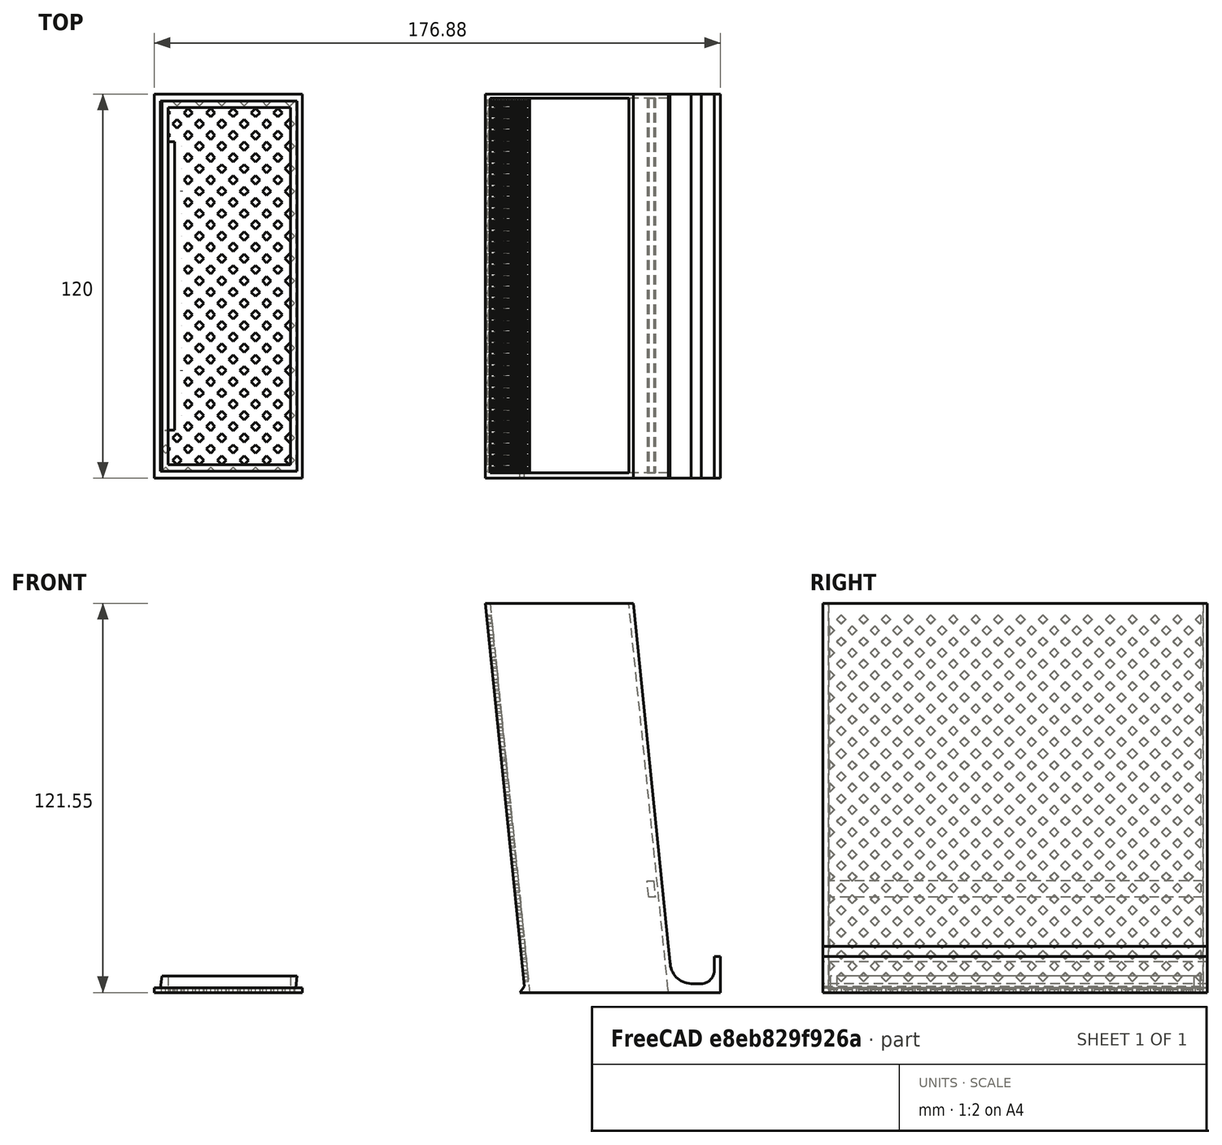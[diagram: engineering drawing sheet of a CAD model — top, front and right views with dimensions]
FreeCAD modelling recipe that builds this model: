
FCSTD DOCUMENT  (FreeCAD 0.18.4R)
Label: container.v3
License: All rights reserved
LicenseURL: http://en.wikipedia.org/wiki/All_rights_reserved
objects: Part::MultiFuse×2, Part::Part2DObjectPython×1, Part::Extrusion×1, Part::Feature×1
note: 5 computed .brp shape members not serialized (recipe doc carries the construction recipe); baked Part::Feature solids carry a one-line shape summary decoded from their .brp

FEATURE [Part::MultiFuse] Fusion004
FEATURE [Part::Part2DObjectPython] Wire  # Draft 2D object (typed FeaturePython)
  ChamferSize = 0
  Closed = true
  End = (105.196,-112.777,-131.382)
  FilletRadius = 0
  Length = 5.87558
  MakeFace = true
  Placement = pos=(104.993,-112.777,-129.392) rot=(1,0,0;1.5708rad)
  Points = (3) [(0,0,0),(-1.29779,-1.98975,-2.84217e-14),(0.202211,-1.98975,-2.84217e-14)]
  Start = (104.993,-112.777,-129.392)
  Subdivisions = 0
FEATURE [Part::Extrusion] Extrusion005
  Base = -> Wire
  Dir = (1.1701e-12,120,1.794e-12)
  DirMode = 0
  FaceMakerClass = Part::FaceMakerBullseye
  LengthFwd = 0
  LengthRev = 0
  Solid = true
  Symmetric = false
FEATURE [Part::MultiFuse] Fusion018002001008013
  Shapes = -> [Extrusion005,Fusion004]
FEATURE [Part::Feature] Fusion018002001008014
  Placement = pos=(1.0587e-12,-240,-121.554) rot=(0,0,1;0rad)
  shape: bbox 46.3 x 120 x 5.151 mm, 1154 faces (baked)
